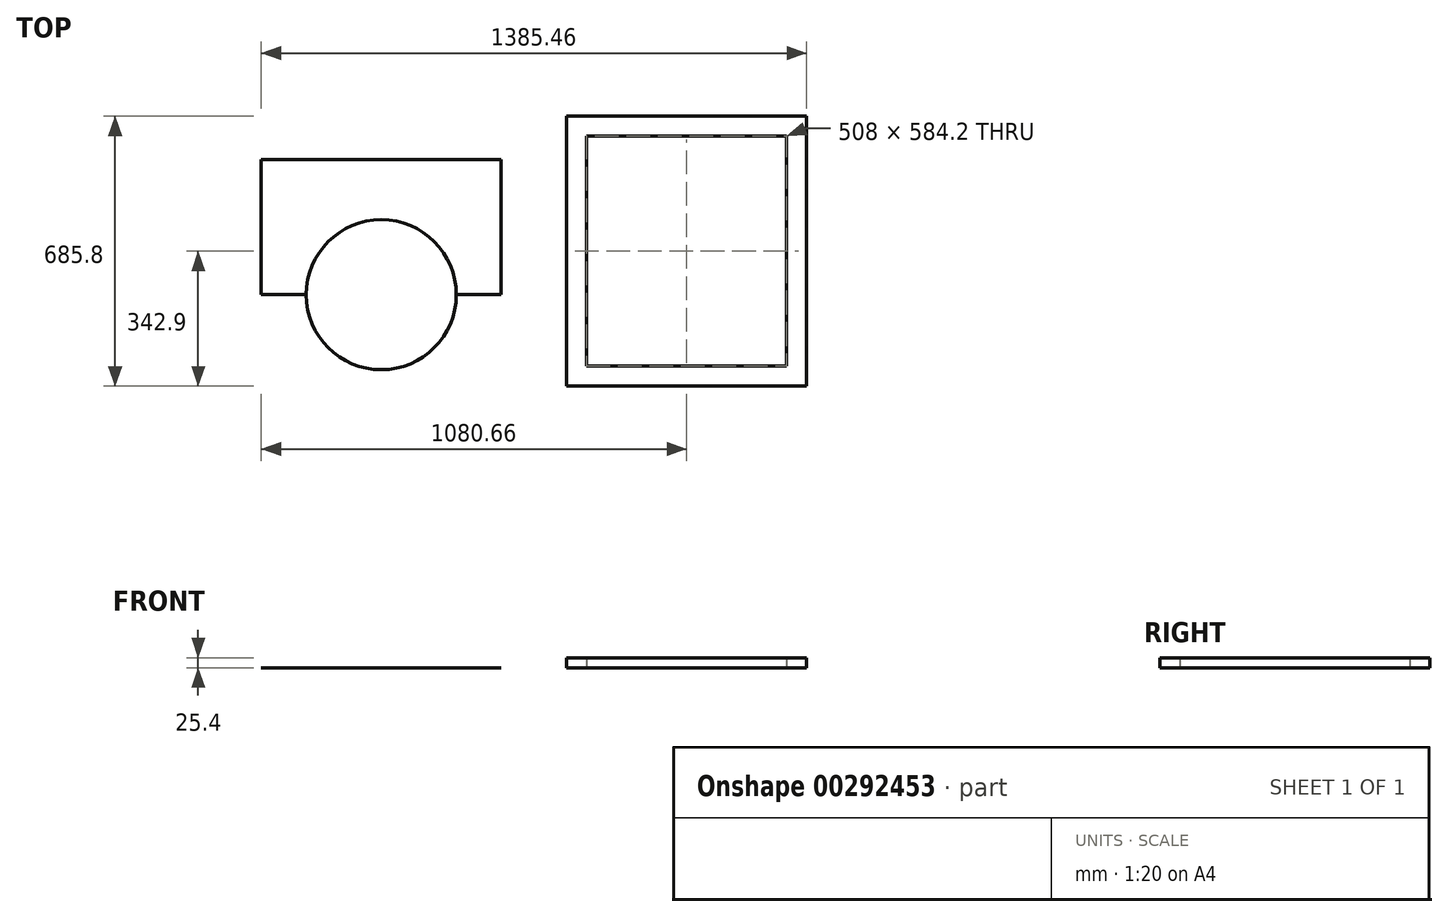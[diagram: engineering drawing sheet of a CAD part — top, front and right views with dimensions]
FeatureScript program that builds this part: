
annotation { "Feature Type Name" : "Feature", "Feature Type Description" : "" }
export const myFeature = defineFeature(function(context is Context, id is Id, definition is map)
    precondition{}
    {
        {
            var Q0;
            Q0=qCreatedBy(makeId("Top.planeOp"),FACE);
            var sketch = newSketch(context, id + "F0", { "sketchPlane" : qUnion([Q0])});
            skLineSegment(sketch, "E0.bottom", {"start": v(-99.1, -161.57) * mm, "end": v(-708.7, -161.57) * mm});
            skLineSegment(sketch, "E0.top", {"start": v(-99.1, 524.23) * mm, "end": v(-708.7, 524.23) * mm});
            skLineSegment(sketch, "E0.left", {"start": v(-99.1, -161.57) * mm, "end": v(-99.1, 524.23) * mm});
            skLineSegment(sketch, "E0.right", {"start": v(-708.7, -161.57) * mm, "end": v(-708.7, 524.23) * mm});
            skPoint(sketch, "E0.middle", {"position": v(-403.9, 181.33) * mm});
            skCircle(sketch, "E1", {"center": v(-403.9, 181.33) * mm, "radius": 190.5 * mm});
            skLineSegment(sketch, "E2", {"start": v(-213.4, 181.33) * mm, "end": v(-99.1, 181.33) * mm});
            skLineSegment(sketch, "E3", {"start": v(-708.7, 181.33) * mm, "end": v(-594.4, 181.33) * mm});
            skSolve(sketch);
        }
        {
            var Q0;
            {var subQ0=sQuery(id+"F0.wireOp",EDGE,"E1");var subQ1=makeQuery(id+"F0.imprint","INTERSECT",VERTEX,{"derivedFrom":[subQ0,sQuery(id+"F0.wireOp",EDGE,"E2")]});Q0=makeQuery(id+"F0.imprint","IMPRINT",FACE,{"disambiguationData":[TD([[makeQuery(id+"F0.imprint","IMPRINT",EDGE,{"disambiguationData":[TD([[subQ1,-1.0]])],"derivedFrom":subQ0}),1.0]])]});}
            extrude(context, id + "F1", {"entities" : qUnion([Q0]), "depth" : 1 / 203.2 * mm});
        }
        {
            var Q0;
            {var subQ1=sQuery(id+"F0.wireOp",EDGE,"E0.top");Q0=makeQuery(id+"F0.imprint","IMPRINT",FACE,{"disambiguationData":[TD([[makeQuery(id+"F0.imprint","IMPRINT",EDGE,{"derivedFrom":subQ1}),1.0]])]});}
            extrude(context, id + "F2", {"entities" : qUnion([Q0]), "depth" : 1 / 203.2 * mm});
        }
        {
            var Q0;
            Q0=qCreatedBy(makeId("Top.planeOp"),FACE);
            var sketch = newSketch(context, id + "F3", { "sketchPlane" : qUnion([Q0])});
            skLineSegment(sketch, "E4.bottom", {"start": v(676.76, -50.9) * mm, "end": v(67.16, -50.9) * mm});
            skLineSegment(sketch, "E4.top", {"start": v(676.76, 634.9) * mm, "end": v(67.16, 634.9) * mm});
            skLineSegment(sketch, "E4.left", {"start": v(676.76, -50.9) * mm, "end": v(676.76, 634.9) * mm});
            skLineSegment(sketch, "E4.right", {"start": v(67.16, -50.9) * mm, "end": v(67.16, 634.9) * mm});
            skPoint(sketch, "E4.middle", {"position": v(371.96, 292) * mm});
            skLineSegment(sketch, "E5.0", {"start": v(117.96, -0.1) * mm, "end": v(117.96, 584.1) * mm});
            skLineSegment(sketch, "E5.1", {"start": v(625.96, -0.1) * mm, "end": v(117.96, -0.1) * mm});
            skLineSegment(sketch, "E5.2", {"start": v(625.96, -0.1) * mm, "end": v(625.96, 584.1) * mm});
            skLineSegment(sketch, "E5.3", {"start": v(625.96, 584.1) * mm, "end": v(117.96, 584.1) * mm});
            skSolve(sketch);
        }
        {
            var Q0;
            Q0=makeQuery(id+"F3.imprint","IMPRINT",FACE,{"disambiguationData":[TD([[makeQuery(id+"F3.imprint","IMPRINT",EDGE,{"derivedFrom":sQuery(id+"F3.wireOp",EDGE,"E4.bottom")}),-1.0]])]});
            extrude(context, id + "F4", {"entities" : qUnion([Q0]), "depth" : 25.4 * mm});
        }
    });
